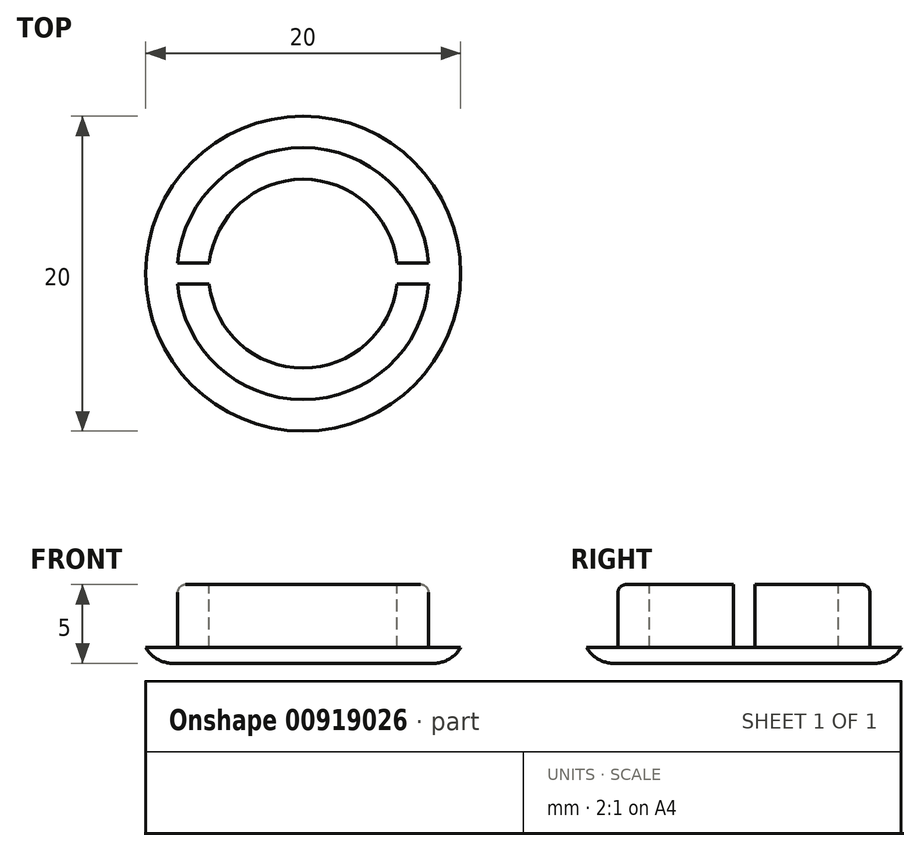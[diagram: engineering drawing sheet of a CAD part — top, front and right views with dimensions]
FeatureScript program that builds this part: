
annotation { "Feature Type Name" : "Feature", "Feature Type Description" : "" }
export const myFeature = defineFeature(function(context is Context, id is Id, definition is map)
    precondition{}
    {
        {
            var Q0;
            Q0=qCreatedBy(makeId("Top.planeOp"),FACE);
            var sketch = newSketch(context, id + "F0", { "sketchPlane" : qUnion([Q0])});
            skCircle(sketch, "E0", {"center": v(0, 0) * mm, "radius": 10 * mm});
            skSolve(sketch);
        }
        {
            var Q0;
            Q0=makeQuery(id+"F0.imprint","IMPRINT",FACE,{"disambiguationData":[TD([[makeQuery(id+"F0.imprint","IMPRINT",EDGE,{"derivedFrom":sQuery(id+"F0.wireOp",EDGE,"E0")}),1.0]])]});
            extrude(context, id + "F1", {"entities" : qUnion([Q0]), "depth" : 1 * mm, "offsetDistance" : 25 * mm});
        }
        {
            var Q0;
            Q0=makeQuery(id+"F1.opExtrude","CAP_EDGE",EDGE,{"disambiguationData":[OSD([sQuery(id+"F0.wireOp",EDGE,"E0")])],"isStart":true});
            fillet(context, id + "F2", {"entities" : qUnion([Q0]), "radius" : 2 * mm, "tangentPropagation" : true, "allowEdgeOverflow" : false});
        }
        {
            var Q0;
            Q0=makeQuery(id+"F1.opExtrude","CAP_FACE",FACE,{"disambiguationData":[OSD([sQuery(id+"F0.wireOp",EDGE,"E0")])],"isStart":false});
            var sketch = newSketch(context, id + "F3", { "sketchPlane" : qUnion([Q0])});
            skCircle(sketch, "E1", {"center": v(0, 0) * mm, "radius": 8 * mm});
            skSolve(sketch);
        }
        {
            var Q0;
            Q0=makeQuery(id+"F3.imprint","IMPRINT",FACE,{"disambiguationData":[TD([[makeQuery(id+"F3.imprint","IMPRINT",EDGE,{"derivedFrom":sQuery(id+"F3.wireOp",EDGE,"E1")}),1.0]])]});
            extrude(context, id + "F4", {"entities" : qUnion([Q0]), "operationType" : NewBodyOperationType.ADD, "depth" : 4 * mm, "offsetDistance" : 25 * mm});
        }
        {
            var Q0;
            Q0=makeQuery(id+"F4.opExtrude","CAP_FACE",FACE,{"disambiguationData":[OSD([sQuery(id+"F3.wireOp",EDGE,"E1")])],"isStart":false});
            var sketch = newSketch(context, id + "F5", { "sketchPlane" : qUnion([Q0])});
            skCircle(sketch, "E2", {"center": v(0, 0) * mm, "radius": 6 * mm});
            skSolve(sketch);
        }
        {
            var Q0;
            Q0=makeQuery(id+"F5.imprint","IMPRINT",FACE,{"disambiguationData":[TD([[makeQuery(id+"F5.imprint","IMPRINT",EDGE,{"derivedFrom":sQuery(id+"F5.wireOp",EDGE,"E2")}),1.0]])]});
            extrude(context, id + "F6", {"entities" : qUnion([Q0]), "operationType" : NewBodyOperationType.REMOVE, "oppositeDirection" : true, "depth" : 4 * mm, "offsetDistance" : 25 * mm});
        }
        {
            var Q0;
            Q0=makeQuery(id+"F6.boolean.opBoolean","COPY",FACE,{"derivedFrom":makeQuery(id+"F6.opExtrude","CAP_FACE",FACE,{"disambiguationData":[OSD([sQuery(id+"F5.wireOp",EDGE,"E2")])],"isStart":false})});
            var sketch = newSketch(context, id + "F7", { "sketchPlane" : qUnion([Q0])});
            skLineSegment(sketch, "E3.bottom", {"start": v(-8.76, -0.67) * mm, "end": v(8.56, -0.67) * mm});
            skLineSegment(sketch, "E3.top", {"start": v(-8.76, 0.68) * mm, "end": v(8.56, 0.68) * mm});
            skLineSegment(sketch, "E3.left", {"start": v(-8.76, -0.67) * mm, "end": v(-8.76, 0.68) * mm});
            skLineSegment(sketch, "E3.right", {"start": v(8.56, -0.67) * mm, "end": v(8.56, 0.68) * mm});
            skSolve(sketch);
        }
        {
            var Q0;
            Q0 = qSketchRegion(id + "F7", true);
            extrude(context, id + "F8", {"entities" : qUnion([Q0]), "operationType" : NewBodyOperationType.REMOVE, "depth" : 25 * mm, "offsetDistance" : 25 * mm});
        }
        {
            var Q0;
            {var subQ0=sQuery(id+"F3.wireOp",EDGE,"E1");Q0=makeQuery(id+"F8.boolean.opBoolean","SPLIT",EDGE,{"disambiguationData":[TD([makeQuery(id+"F8.opExtrude","SWEPT_FACE",FACE,{"disambiguationData":[OSD([sQuery(id+"F7.wireOp",EDGE,"E3.top")])]})])],"derivedFrom":makeQuery(id+"F4.opExtrude","CAP_EDGE",EDGE,{"disambiguationData":[OSD([subQ0])],"isStart":false})});}
            var Q1;
            {var subQ0=sQuery(id+"F3.wireOp",EDGE,"E1");Q1=makeQuery(id+"F8.boolean.opBoolean","SPLIT",EDGE,{"disambiguationData":[TD([makeQuery(id+"F8.opExtrude","SWEPT_FACE",FACE,{"disambiguationData":[OSD([sQuery(id+"F7.wireOp",EDGE,"E3.bottom")])]})])],"derivedFrom":makeQuery(id+"F4.opExtrude","CAP_EDGE",EDGE,{"disambiguationData":[OSD([subQ0])],"isStart":false})});}
            fillet(context, id + "F9", {"entities" : qUnion([Q0, Q1]), "radius" : 0.5 * mm, "tangentPropagation" : true, "allowEdgeOverflow" : false});
        }
    });
